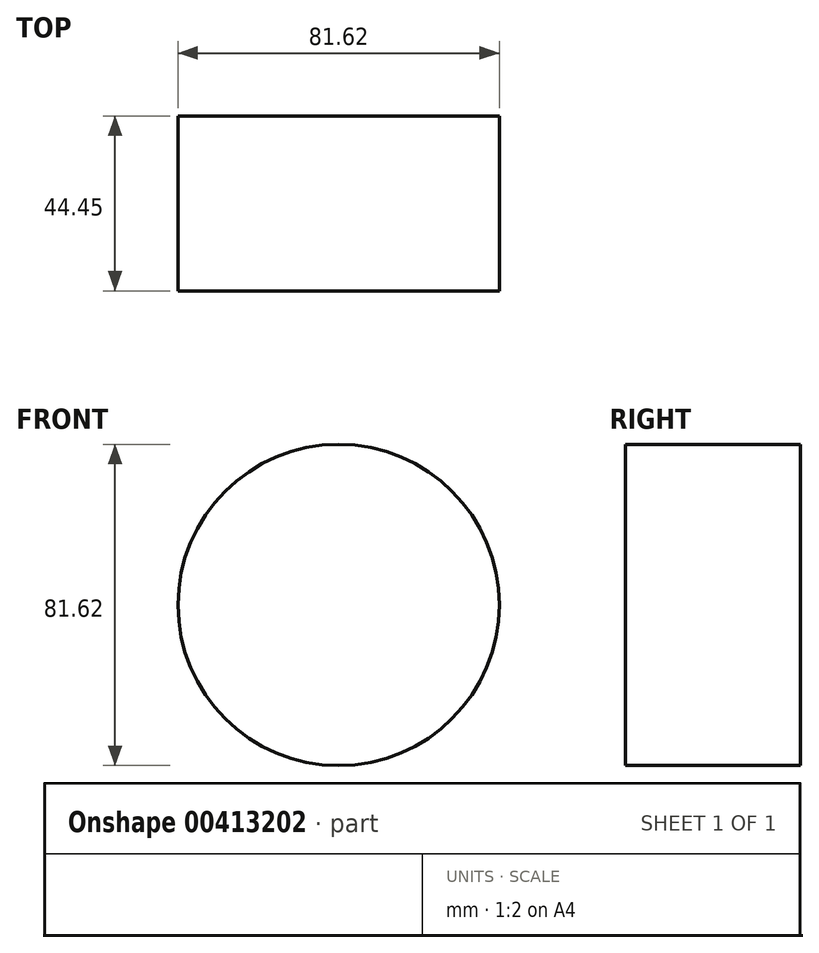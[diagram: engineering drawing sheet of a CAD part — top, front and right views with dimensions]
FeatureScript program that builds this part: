
annotation { "Feature Type Name" : "Feature", "Feature Type Description" : "" }
export const myFeature = defineFeature(function(context is Context, id is Id, definition is map)
    precondition{}
    {
        {
            var Q0;
            Q0=qCreatedBy(makeId("Front.planeOp"),FACE);
            var sketch = newSketch(context, id + "F0", { "sketchPlane" : qUnion([Q0])});
            skCircle(sketch, "E0", {"center": v(0, 0) * mm, "radius": 40.81 * mm});
            skSolve(sketch);
        }
        {
            var Q0;
            Q0 = qSketchRegion(id + "F0", true);
            extrude(context, id + "F1", {"entities" : qUnion([Q0]), "depth" : 44.45 * mm});
        }
    });
